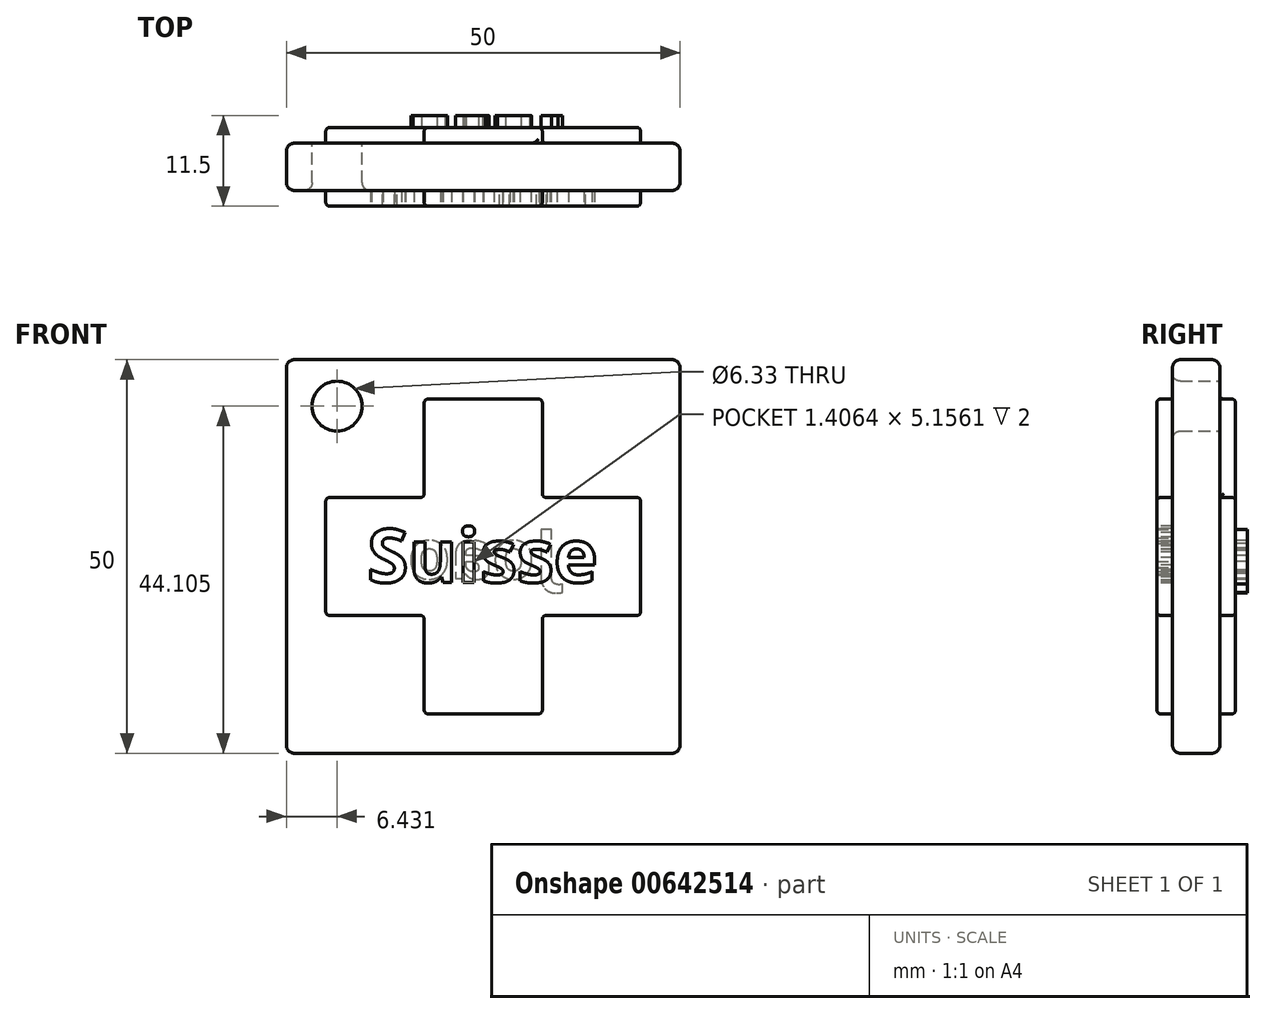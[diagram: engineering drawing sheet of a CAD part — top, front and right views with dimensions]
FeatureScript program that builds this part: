
annotation { "Feature Type Name" : "Feature", "Feature Type Description" : "" }
export const myFeature = defineFeature(function(context is Context, id is Id, definition is map)
    precondition{}
    {
        {
            var Q0;
            Q0=qCreatedBy(makeId("Front.planeOp"),FACE);
            var sketch = newSketch(context, id + "F0", { "sketchPlane" : qUnion([Q0])});
            skLineSegment(sketch, "E0.bottom", {"start": v(25, -25) * mm, "end": v(-25, -25) * mm});
            skLineSegment(sketch, "E0.top", {"start": v(25, 25) * mm, "end": v(-25, 25) * mm});
            skLineSegment(sketch, "E0.left", {"start": v(25, -25) * mm, "end": v(25, 25) * mm});
            skLineSegment(sketch, "E0.right", {"start": v(-25, -25) * mm, "end": v(-25, 25) * mm});
            skLineSegment(sketch, "E1.bottom", {"start": v(7.5, -20) * mm, "end": v(-7.5, -20) * mm});
            skLineSegment(sketch, "E1.top", {"start": v(7.5, 20) * mm, "end": v(-7.5, 20) * mm});
            skLineSegment(sketch, "E1.left", {"start": v(7.5, -20) * mm, "end": v(7.5, 20) * mm});
            skLineSegment(sketch, "E1.right", {"start": v(-7.5, -20) * mm, "end": v(-7.5, 20) * mm});
            skPoint(sketch, "E1.middle", {"position": v(0, 0) * mm});
            skLineSegment(sketch, "E2.bottom", {"start": v(-20, 7.5) * mm, "end": v(20, 7.5) * mm});
            skLineSegment(sketch, "E2.top", {"start": v(-20, -7.5) * mm, "end": v(20, -7.5) * mm});
            skLineSegment(sketch, "E2.left", {"start": v(-20, 7.5) * mm, "end": v(-20, -7.5) * mm});
            skLineSegment(sketch, "E2.right", {"start": v(20, 7.5) * mm, "end": v(20, -7.5) * mm});
            skSolve(sketch);
        }
        {
            var Q0;
            {var subQ0=sQuery(id+"F0.wireOp",EDGE,"E2.top");var subQ1=sQuery(id+"F0.wireOp",EDGE,"E1.left");var subQ2=makeQuery(id+"F0.imprint","INTERSECT",VERTEX,{"derivedFrom":[subQ1,subQ0]});Q0=makeQuery(id+"F0.imprint","IMPRINT",FACE,{"disambiguationData":[TD([[makeQuery(id+"F0.imprint","IMPRINT",EDGE,{"disambiguationData":[TD([[subQ2,-1.0]])],"derivedFrom":subQ1}),1.0]])]});}
            var Q1;
            {var subQ5=sQuery(id+"F0.wireOp",EDGE,"E2.left");Q1=makeQuery(id+"F0.imprint","IMPRINT",FACE,{"disambiguationData":[TD([[makeQuery(id+"F0.imprint","IMPRINT",EDGE,{"derivedFrom":subQ5}),1.0]])]});}
            var Q2;
            {var subQ5=sQuery(id+"F0.wireOp",EDGE,"E2.right");Q2=makeQuery(id+"F0.imprint","IMPRINT",FACE,{"disambiguationData":[TD([[makeQuery(id+"F0.imprint","IMPRINT",EDGE,{"derivedFrom":subQ5}),-1.0]])]});}
            var Q3;
            {var subQ0=sQuery(id+"F0.wireOp",EDGE,"E1.bottom");Q3=makeQuery(id+"F0.imprint","IMPRINT",FACE,{"disambiguationData":[TD([[makeQuery(id+"F0.imprint","IMPRINT",EDGE,{"derivedFrom":subQ0}),-1.0]])]});}
            var Q4;
            {var subQ0=sQuery(id+"F0.wireOp",EDGE,"E1.top");Q4=makeQuery(id+"F0.imprint","IMPRINT",FACE,{"disambiguationData":[TD([[makeQuery(id+"F0.imprint","IMPRINT",EDGE,{"derivedFrom":subQ0}),1.0]])]});}
            extrude(context, id + "F1", {"entities" : qUnion([Q0, Q1, Q2, Q3, Q4]), "endBound" : BoundingType.SYMMETRIC, "depth" : 10 * mm, "offsetDistance" : 25 * mm});
        }
        {
            var Q0;
            Q0=makeQuery(id+"F0.imprint","IMPRINT",FACE,{"disambiguationData":[TD([[makeQuery(id+"F0.imprint","IMPRINT",EDGE,{"derivedFrom":sQuery(id+"F0.wireOp",EDGE,"E0.bottom")}),-1.0]])]});
            extrude(context, id + "F2", {"entities" : qUnion([Q0]), "operationType" : NewBodyOperationType.ADD, "endBound" : BoundingType.SYMMETRIC, "depth" : 6 * mm, "offsetDistance" : 25 * mm});
        }
        {
            var Q0;
            Q0=makeQuery(id+"F1.opExtrude","CAP_FACE",FACE,{"disambiguationData":[OSD([sQuery(id+"F0.wireOp",EDGE,"E1.bottom"),sQuery(id+"F0.wireOp",EDGE,"E1.top"),sQuery(id+"F0.wireOp",EDGE,"E1.left"),sQuery(id+"F0.wireOp",EDGE,"E1.right"),sQuery(id+"F0.wireOp",EDGE,"E2.bottom"),sQuery(id+"F0.wireOp",EDGE,"E2.top"),sQuery(id+"F0.wireOp",EDGE,"E2.left"),sQuery(id+"F0.wireOp",EDGE,"E2.right")])],"isStart":true});
            var sketch = newSketch(context, id + "F3", { "sketchPlane" : qUnion([Q0])});
            skText(sketch, "E3", { "text": "Joao", "fontName": "OpenSans-Bold.ttf"});
            const initialGuessF3  = {"E3": [-0.00944, -0.00282, 1, 0, 0.0063]};
            skSetInitialGuess(sketch, initialGuessF3);
            skSolve(sketch);
        }
        {
            var Q0;
            Q0 = qSketchRegion(id + "F3", true);
            extrude(context, id + "F4", {"entities" : qUnion([Q0]), "operationType" : NewBodyOperationType.ADD, "endBound" : BoundingType.SYMMETRIC, "depth" : 3 * mm, "offsetDistance" : 25 * mm});
        }
        {
            var Q0;
            Q0=makeQuery(id+"F2.opExtrude","CAP_FACE",FACE,{"disambiguationData":[OSD([sQuery(id+"F0.wireOp",EDGE,"E0.bottom"),sQuery(id+"F0.wireOp",EDGE,"E0.top"),sQuery(id+"F0.wireOp",EDGE,"E0.left"),sQuery(id+"F0.wireOp",EDGE,"E0.right"),sQuery(id+"F0.wireOp",EDGE,"E1.bottom"),sQuery(id+"F0.wireOp",EDGE,"E1.top"),sQuery(id+"F0.wireOp",EDGE,"E1.left"),sQuery(id+"F0.wireOp",EDGE,"E1.right"),sQuery(id+"F0.wireOp",EDGE,"E2.bottom"),sQuery(id+"F0.wireOp",EDGE,"E2.top"),sQuery(id+"F0.wireOp",EDGE,"E2.left"),sQuery(id+"F0.wireOp",EDGE,"E2.right")])],"isStart":true});
            var sketch = newSketch(context, id + "F5", { "sketchPlane" : qUnion([Q0])});
            skCircle(sketch, "E4", {"center": v(18.57, 19.1) * mm, "radius": 3.17 * mm});
            skSolve(sketch);
        }
        {
            var Q0;
            Q0 = qSketchRegion(id + "F5", true);
            extrude(context, id + "F6", {"entities" : qUnion([Q0]), "operationType" : NewBodyOperationType.REMOVE, "oppositeDirection" : true, "depth" : 25 * mm, "offsetDistance" : 25 * mm});
        }
        {
            var Q0;
            Q0=makeQuery(id+"F2.opExtrude","CAP_EDGE",EDGE,{"disambiguationData":[OSD([sQuery(id+"F0.wireOp",EDGE,"E0.bottom")])],"isStart":false});
            var Q1;
            Q1=makeQuery(id+"F2.opExtrude","CAP_EDGE",EDGE,{"disambiguationData":[OSD([sQuery(id+"F0.wireOp",EDGE,"E0.left")])],"isStart":false});
            var Q2;
            Q2=makeQuery(id+"F2.opExtrude","CAP_EDGE",EDGE,{"disambiguationData":[OSD([sQuery(id+"F0.wireOp",EDGE,"E0.right")])],"isStart":false});
            var Q3;
            Q3=makeQuery(id+"F2.opExtrude","CAP_EDGE",EDGE,{"disambiguationData":[OSD([sQuery(id+"F0.wireOp",EDGE,"E0.top")])],"isStart":false});
            var Q4;
            Q4=makeQuery(id+"F2.opExtrude","SWEPT_EDGE",EDGE,{"disambiguationData":[OSD([sQuery(id+"F0.wireOp",EDGE,"E0.top"),sQuery(id+"F0.wireOp",EDGE,"E0.left")])]});
            var Q5;
            Q5=makeQuery(id+"F2.opExtrude","SWEPT_EDGE",EDGE,{"disambiguationData":[OSD([sQuery(id+"F0.wireOp",EDGE,"E0.bottom"),sQuery(id+"F0.wireOp",EDGE,"E0.left")])]});
            var Q6;
            Q6=makeQuery(id+"F2.opExtrude","SWEPT_EDGE",EDGE,{"disambiguationData":[OSD([sQuery(id+"F0.wireOp",EDGE,"E0.bottom"),sQuery(id+"F0.wireOp",EDGE,"E0.right")])]});
            var Q7;
            Q7=makeQuery(id+"F2.opExtrude","SWEPT_EDGE",EDGE,{"disambiguationData":[OSD([sQuery(id+"F0.wireOp",EDGE,"E0.top"),sQuery(id+"F0.wireOp",EDGE,"E0.right")])]});
            var Q8;
            Q8=makeQuery(id+"F2.opExtrude","CAP_EDGE",EDGE,{"disambiguationData":[OSD([sQuery(id+"F0.wireOp",EDGE,"E0.top")])],"isStart":true});
            var Q9;
            Q9=makeQuery(id+"F2.opExtrude","CAP_EDGE",EDGE,{"disambiguationData":[OSD([sQuery(id+"F0.wireOp",EDGE,"E0.right")])],"isStart":true});
            var Q10;
            Q10=makeQuery(id+"F2.opExtrude","CAP_EDGE",EDGE,{"disambiguationData":[OSD([sQuery(id+"F0.wireOp",EDGE,"E0.left")])],"isStart":true});
            var Q11;
            Q11=makeQuery(id+"F2.opExtrude","CAP_EDGE",EDGE,{"disambiguationData":[OSD([sQuery(id+"F0.wireOp",EDGE,"E0.bottom")])],"isStart":true});
            var Q12;
            Q12=makeQuery(id+"F6.boolean.opBoolean","COPY",EDGE,{"derivedFrom":makeQuery(id+"F6.opExtrude","CAP_EDGE",EDGE,{"disambiguationData":[OSD([sQuery(id+"F5.wireOp",EDGE,"E4")])],"isStart":true})});
            var Q13;
            Q13=makeQuery(id+"F6.boolean.opBoolean","INTERSECT",EDGE,{"derivedFrom":[makeQuery(id+"F2.opExtrude","CAP_FACE",FACE,{"disambiguationData":[OSD([sQuery(id+"F0.wireOp",EDGE,"E0.bottom"),sQuery(id+"F0.wireOp",EDGE,"E0.top"),sQuery(id+"F0.wireOp",EDGE,"E0.left"),sQuery(id+"F0.wireOp",EDGE,"E0.right"),sQuery(id+"F0.wireOp",EDGE,"E1.bottom"),sQuery(id+"F0.wireOp",EDGE,"E1.top"),sQuery(id+"F0.wireOp",EDGE,"E1.left"),sQuery(id+"F0.wireOp",EDGE,"E1.right"),sQuery(id+"F0.wireOp",EDGE,"E2.bottom"),sQuery(id+"F0.wireOp",EDGE,"E2.top"),sQuery(id+"F0.wireOp",EDGE,"E2.left"),sQuery(id+"F0.wireOp",EDGE,"E2.right")])],"isStart":false}),makeQuery(id+"F6.opExtrude","SWEPT_FACE",FACE,{"disambiguationData":[OSD([sQuery(id+"F5.wireOp",EDGE,"E4")])]})]});
            fillet(context, id + "F7", {"entities" : qUnion([Q0, Q1, Q2, Q3, Q4, Q5, Q6, Q7, Q8, Q9, Q10, Q11, Q12, Q13]), "radius" : 1 * mm, "tangentPropagation" : true, "allowEdgeOverflow" : false});
        }
        {
            var Q0;
            Q0=makeQuery(id+"F1.opExtrude","CAP_EDGE",EDGE,{"disambiguationData":[OSD([sQuery(id+"F0.wireOp",EDGE,"E2.left")])],"isStart":false});
            var Q1;
            {var subQ0=sQuery(id+"F0.wireOp",EDGE,"E2.right");var subQ1=sQuery(id+"F0.wireOp",EDGE,"E2.left");var subQ2=sQuery(id+"F0.wireOp",EDGE,"E2.top");var subQ3=sQuery(id+"F0.wireOp",EDGE,"E2.bottom");var subQ4=sQuery(id+"F0.wireOp",EDGE,"E1.right");var subQ5=sQuery(id+"F0.wireOp",EDGE,"E1.left");var subQ6=sQuery(id+"F0.wireOp",EDGE,"E1.top");var subQ7=sQuery(id+"F0.wireOp",EDGE,"E1.bottom");Q1=makeQuery(id+"F2.boolean.opBoolean","SPLIT",EDGE,{"disambiguationData":[TD([makeQuery(id+"F1.opExtrude","CAP_FACE",FACE,{"disambiguationData":[OSD([subQ7,subQ6,subQ5,subQ4,subQ3,subQ2,subQ1,subQ0])],"isStart":false})])],"derivedFrom":makeQuery(id+"F1.opExtrude","SWEPT_EDGE",EDGE,{"disambiguationData":[OSD([subQ3,subQ1])]})});}
            var Q2;
            {var subQ0=sQuery(id+"F0.wireOp",EDGE,"E2.bottom");Q2=makeQuery(id+"F1.opExtrude","CAP_EDGE",EDGE,{"disambiguationData":[OSD([subQ0]),TDD([makeQuery(id+"F0.imprint","IMPRINT",EDGE,{"disambiguationData":[TD([[makeQuery(id+"F0.imprint","INTERSECT",VERTEX,{"derivedFrom":[subQ0,sQuery(id+"F0.wireOp",EDGE,"E2.left")]}),-1.0]])],"derivedFrom":subQ0})])],"isStart":false});}
            var Q3;
            {var subQ0=sQuery(id+"F0.wireOp",EDGE,"E2.top");Q3=makeQuery(id+"F1.opExtrude","CAP_EDGE",EDGE,{"disambiguationData":[OSD([subQ0]),TDD([makeQuery(id+"F0.imprint","IMPRINT",EDGE,{"disambiguationData":[TD([[makeQuery(id+"F0.imprint","INTERSECT",VERTEX,{"derivedFrom":[subQ0,sQuery(id+"F0.wireOp",EDGE,"E2.left")]}),-1.0]])],"derivedFrom":subQ0})])],"isStart":false});}
            var Q4;
            {var subQ0=sQuery(id+"F0.wireOp",EDGE,"E1.right");Q4=makeQuery(id+"F1.opExtrude","CAP_EDGE",EDGE,{"disambiguationData":[OSD([subQ0]),TDD([makeQuery(id+"F0.imprint","IMPRINT",EDGE,{"disambiguationData":[TD([[makeQuery(id+"F0.imprint","INTERSECT",VERTEX,{"derivedFrom":[sQuery(id+"F0.wireOp",EDGE,"E1.bottom"),subQ0]}),-1.0]])],"derivedFrom":subQ0})])],"isStart":false});}
            var Q5;
            {var subQ0=sQuery(id+"F0.wireOp",EDGE,"E2.right");var subQ1=sQuery(id+"F0.wireOp",EDGE,"E2.left");var subQ2=sQuery(id+"F0.wireOp",EDGE,"E2.top");var subQ3=sQuery(id+"F0.wireOp",EDGE,"E2.bottom");var subQ4=sQuery(id+"F0.wireOp",EDGE,"E1.right");var subQ5=sQuery(id+"F0.wireOp",EDGE,"E1.left");var subQ6=sQuery(id+"F0.wireOp",EDGE,"E1.top");var subQ7=sQuery(id+"F0.wireOp",EDGE,"E1.bottom");Q5=makeQuery(id+"F2.boolean.opBoolean","SPLIT",EDGE,{"disambiguationData":[TD([makeQuery(id+"F1.opExtrude","CAP_FACE",FACE,{"disambiguationData":[OSD([subQ7,subQ6,subQ5,subQ4,subQ3,subQ2,subQ1,subQ0])],"isStart":false})])],"derivedFrom":makeQuery(id+"F1.opExtrude","SWEPT_EDGE",EDGE,{"disambiguationData":[OSD([subQ4,subQ2])]})});}
            var Q6;
            {var subQ0=sQuery(id+"F0.wireOp",EDGE,"E2.right");var subQ1=sQuery(id+"F0.wireOp",EDGE,"E2.left");var subQ2=sQuery(id+"F0.wireOp",EDGE,"E2.top");var subQ3=sQuery(id+"F0.wireOp",EDGE,"E2.bottom");var subQ4=sQuery(id+"F0.wireOp",EDGE,"E1.right");var subQ5=sQuery(id+"F0.wireOp",EDGE,"E1.left");var subQ6=sQuery(id+"F0.wireOp",EDGE,"E1.top");var subQ7=sQuery(id+"F0.wireOp",EDGE,"E1.bottom");Q6=makeQuery(id+"F2.boolean.opBoolean","SPLIT",EDGE,{"disambiguationData":[TD([makeQuery(id+"F1.opExtrude","CAP_FACE",FACE,{"disambiguationData":[OSD([subQ7,subQ6,subQ5,subQ4,subQ3,subQ2,subQ1,subQ0])],"isStart":false})])],"derivedFrom":makeQuery(id+"F1.opExtrude","SWEPT_EDGE",EDGE,{"disambiguationData":[OSD([subQ2,subQ1])]})});}
            var Q7;
            Q7=makeQuery(id+"F1.opExtrude","CAP_EDGE",EDGE,{"disambiguationData":[OSD([sQuery(id+"F0.wireOp",EDGE,"E1.bottom")])],"isStart":false});
            var Q8;
            {var subQ0=sQuery(id+"F0.wireOp",EDGE,"E1.bottom");var subQ1=sQuery(id+"F0.wireOp",EDGE,"E2.right");var subQ2=sQuery(id+"F0.wireOp",EDGE,"E2.left");var subQ3=sQuery(id+"F0.wireOp",EDGE,"E2.top");var subQ4=sQuery(id+"F0.wireOp",EDGE,"E2.bottom");var subQ5=sQuery(id+"F0.wireOp",EDGE,"E1.right");var subQ6=sQuery(id+"F0.wireOp",EDGE,"E1.left");var subQ7=sQuery(id+"F0.wireOp",EDGE,"E1.top");Q8=makeQuery(id+"F2.boolean.opBoolean","SPLIT",EDGE,{"disambiguationData":[TD([makeQuery(id+"F1.opExtrude","CAP_FACE",FACE,{"disambiguationData":[OSD([subQ0,subQ7,subQ6,subQ5,subQ4,subQ3,subQ2,subQ1])],"isStart":false})])],"derivedFrom":makeQuery(id+"F1.opExtrude","SWEPT_EDGE",EDGE,{"disambiguationData":[OSD([subQ0,subQ5])]})});}
            var Q9;
            {var subQ0=sQuery(id+"F0.wireOp",EDGE,"E1.left");Q9=makeQuery(id+"F1.opExtrude","CAP_EDGE",EDGE,{"disambiguationData":[OSD([subQ0]),TDD([makeQuery(id+"F0.imprint","IMPRINT",EDGE,{"disambiguationData":[TD([[makeQuery(id+"F0.imprint","INTERSECT",VERTEX,{"derivedFrom":[sQuery(id+"F0.wireOp",EDGE,"E1.bottom"),subQ0]}),-1.0]])],"derivedFrom":subQ0})])],"isStart":false});}
            var Q10;
            {var subQ0=sQuery(id+"F0.wireOp",EDGE,"E2.top");Q10=makeQuery(id+"F1.opExtrude","CAP_EDGE",EDGE,{"disambiguationData":[OSD([subQ0]),TDD([makeQuery(id+"F0.imprint","IMPRINT",EDGE,{"disambiguationData":[TD([[makeQuery(id+"F0.imprint","INTERSECT",VERTEX,{"derivedFrom":[subQ0,sQuery(id+"F0.wireOp",EDGE,"E2.right")]}),1.0]])],"derivedFrom":subQ0})])],"isStart":false});}
            var Q11;
            {var subQ0=sQuery(id+"F0.wireOp",EDGE,"E2.right");var subQ1=sQuery(id+"F0.wireOp",EDGE,"E2.left");var subQ2=sQuery(id+"F0.wireOp",EDGE,"E2.top");var subQ3=sQuery(id+"F0.wireOp",EDGE,"E2.bottom");var subQ4=sQuery(id+"F0.wireOp",EDGE,"E1.right");var subQ5=sQuery(id+"F0.wireOp",EDGE,"E1.left");var subQ6=sQuery(id+"F0.wireOp",EDGE,"E1.top");var subQ7=sQuery(id+"F0.wireOp",EDGE,"E1.bottom");Q11=makeQuery(id+"F2.boolean.opBoolean","SPLIT",EDGE,{"disambiguationData":[TD([makeQuery(id+"F1.opExtrude","CAP_FACE",FACE,{"disambiguationData":[OSD([subQ7,subQ6,subQ5,subQ4,subQ3,subQ2,subQ1,subQ0])],"isStart":false})])],"derivedFrom":makeQuery(id+"F1.opExtrude","SWEPT_EDGE",EDGE,{"disambiguationData":[OSD([subQ5,subQ2])]})});}
            var Q12;
            {var subQ0=sQuery(id+"F0.wireOp",EDGE,"E1.bottom");var subQ1=sQuery(id+"F0.wireOp",EDGE,"E2.right");var subQ2=sQuery(id+"F0.wireOp",EDGE,"E2.left");var subQ3=sQuery(id+"F0.wireOp",EDGE,"E2.top");var subQ4=sQuery(id+"F0.wireOp",EDGE,"E2.bottom");var subQ5=sQuery(id+"F0.wireOp",EDGE,"E1.right");var subQ6=sQuery(id+"F0.wireOp",EDGE,"E1.left");var subQ7=sQuery(id+"F0.wireOp",EDGE,"E1.top");Q12=makeQuery(id+"F2.boolean.opBoolean","SPLIT",EDGE,{"disambiguationData":[TD([makeQuery(id+"F1.opExtrude","CAP_FACE",FACE,{"disambiguationData":[OSD([subQ0,subQ7,subQ6,subQ5,subQ4,subQ3,subQ2,subQ1])],"isStart":false})])],"derivedFrom":makeQuery(id+"F1.opExtrude","SWEPT_EDGE",EDGE,{"disambiguationData":[OSD([subQ0,subQ6])]})});}
            var Q13;
            {var subQ0=sQuery(id+"F0.wireOp",EDGE,"E2.right");var subQ1=sQuery(id+"F0.wireOp",EDGE,"E2.left");var subQ2=sQuery(id+"F0.wireOp",EDGE,"E2.top");var subQ3=sQuery(id+"F0.wireOp",EDGE,"E2.bottom");var subQ4=sQuery(id+"F0.wireOp",EDGE,"E1.right");var subQ5=sQuery(id+"F0.wireOp",EDGE,"E1.left");var subQ6=sQuery(id+"F0.wireOp",EDGE,"E1.top");var subQ7=sQuery(id+"F0.wireOp",EDGE,"E1.bottom");Q13=makeQuery(id+"F2.boolean.opBoolean","SPLIT",EDGE,{"disambiguationData":[TD([makeQuery(id+"F1.opExtrude","CAP_FACE",FACE,{"disambiguationData":[OSD([subQ7,subQ6,subQ5,subQ4,subQ3,subQ2,subQ1,subQ0])],"isStart":false})])],"derivedFrom":makeQuery(id+"F1.opExtrude","SWEPT_EDGE",EDGE,{"disambiguationData":[OSD([subQ2,subQ0])]})});}
            var Q14;
            Q14=makeQuery(id+"F1.opExtrude","CAP_EDGE",EDGE,{"disambiguationData":[OSD([sQuery(id+"F0.wireOp",EDGE,"E2.right")])],"isStart":false});
            var Q15;
            {var subQ0=sQuery(id+"F0.wireOp",EDGE,"E2.right");var subQ1=sQuery(id+"F0.wireOp",EDGE,"E2.left");var subQ2=sQuery(id+"F0.wireOp",EDGE,"E2.top");var subQ3=sQuery(id+"F0.wireOp",EDGE,"E2.bottom");var subQ4=sQuery(id+"F0.wireOp",EDGE,"E1.right");var subQ5=sQuery(id+"F0.wireOp",EDGE,"E1.left");var subQ6=sQuery(id+"F0.wireOp",EDGE,"E1.top");var subQ7=sQuery(id+"F0.wireOp",EDGE,"E1.bottom");Q15=makeQuery(id+"F2.boolean.opBoolean","SPLIT",EDGE,{"disambiguationData":[TD([makeQuery(id+"F1.opExtrude","CAP_FACE",FACE,{"disambiguationData":[OSD([subQ7,subQ6,subQ5,subQ4,subQ3,subQ2,subQ1,subQ0])],"isStart":false})])],"derivedFrom":makeQuery(id+"F1.opExtrude","SWEPT_EDGE",EDGE,{"disambiguationData":[OSD([subQ3,subQ0])]})});}
            var Q16;
            {var subQ0=sQuery(id+"F0.wireOp",EDGE,"E2.bottom");Q16=makeQuery(id+"F1.opExtrude","CAP_EDGE",EDGE,{"disambiguationData":[OSD([subQ0]),TDD([makeQuery(id+"F0.imprint","IMPRINT",EDGE,{"disambiguationData":[TD([[makeQuery(id+"F0.imprint","INTERSECT",VERTEX,{"derivedFrom":[subQ0,sQuery(id+"F0.wireOp",EDGE,"E2.right")]}),1.0]])],"derivedFrom":subQ0})])],"isStart":false});}
            var Q17;
            {var subQ0=sQuery(id+"F0.wireOp",EDGE,"E2.right");var subQ1=sQuery(id+"F0.wireOp",EDGE,"E2.left");var subQ2=sQuery(id+"F0.wireOp",EDGE,"E2.top");var subQ3=sQuery(id+"F0.wireOp",EDGE,"E2.bottom");var subQ4=sQuery(id+"F0.wireOp",EDGE,"E1.right");var subQ5=sQuery(id+"F0.wireOp",EDGE,"E1.left");var subQ6=sQuery(id+"F0.wireOp",EDGE,"E1.top");var subQ7=sQuery(id+"F0.wireOp",EDGE,"E1.bottom");Q17=makeQuery(id+"F2.boolean.opBoolean","SPLIT",EDGE,{"disambiguationData":[TD([makeQuery(id+"F1.opExtrude","CAP_FACE",FACE,{"disambiguationData":[OSD([subQ7,subQ6,subQ5,subQ4,subQ3,subQ2,subQ1,subQ0])],"isStart":false})])],"derivedFrom":makeQuery(id+"F1.opExtrude","SWEPT_EDGE",EDGE,{"disambiguationData":[OSD([subQ5,subQ3])]})});}
            var Q18;
            {var subQ0=sQuery(id+"F0.wireOp",EDGE,"E1.left");Q18=makeQuery(id+"F1.opExtrude","CAP_EDGE",EDGE,{"disambiguationData":[OSD([subQ0]),TDD([makeQuery(id+"F0.imprint","IMPRINT",EDGE,{"disambiguationData":[TD([[makeQuery(id+"F0.imprint","INTERSECT",VERTEX,{"derivedFrom":[sQuery(id+"F0.wireOp",EDGE,"E1.top"),subQ0]}),1.0]])],"derivedFrom":subQ0})])],"isStart":false});}
            var Q19;
            {var subQ0=sQuery(id+"F0.wireOp",EDGE,"E2.right");var subQ1=sQuery(id+"F0.wireOp",EDGE,"E2.left");var subQ2=sQuery(id+"F0.wireOp",EDGE,"E2.top");var subQ3=sQuery(id+"F0.wireOp",EDGE,"E2.bottom");var subQ4=sQuery(id+"F0.wireOp",EDGE,"E1.right");var subQ5=sQuery(id+"F0.wireOp",EDGE,"E1.left");var subQ6=sQuery(id+"F0.wireOp",EDGE,"E1.top");var subQ7=sQuery(id+"F0.wireOp",EDGE,"E1.bottom");Q19=makeQuery(id+"F2.boolean.opBoolean","SPLIT",EDGE,{"disambiguationData":[TD([makeQuery(id+"F1.opExtrude","CAP_FACE",FACE,{"disambiguationData":[OSD([subQ7,subQ6,subQ5,subQ4,subQ3,subQ2,subQ1,subQ0])],"isStart":false})])],"derivedFrom":makeQuery(id+"F1.opExtrude","SWEPT_EDGE",EDGE,{"disambiguationData":[OSD([subQ6,subQ5])]})});}
            var Q20;
            Q20=makeQuery(id+"F1.opExtrude","CAP_EDGE",EDGE,{"disambiguationData":[OSD([sQuery(id+"F0.wireOp",EDGE,"E1.top")])],"isStart":false});
            var Q21;
            {var subQ0=sQuery(id+"F0.wireOp",EDGE,"E1.right");Q21=makeQuery(id+"F1.opExtrude","CAP_EDGE",EDGE,{"disambiguationData":[OSD([subQ0]),TDD([makeQuery(id+"F0.imprint","IMPRINT",EDGE,{"disambiguationData":[TD([[makeQuery(id+"F0.imprint","INTERSECT",VERTEX,{"derivedFrom":[sQuery(id+"F0.wireOp",EDGE,"E1.top"),subQ0]}),1.0]])],"derivedFrom":subQ0})])],"isStart":false});}
            var Q22;
            {var subQ0=sQuery(id+"F0.wireOp",EDGE,"E2.right");var subQ1=sQuery(id+"F0.wireOp",EDGE,"E2.left");var subQ2=sQuery(id+"F0.wireOp",EDGE,"E2.top");var subQ3=sQuery(id+"F0.wireOp",EDGE,"E2.bottom");var subQ4=sQuery(id+"F0.wireOp",EDGE,"E1.right");var subQ5=sQuery(id+"F0.wireOp",EDGE,"E1.left");var subQ6=sQuery(id+"F0.wireOp",EDGE,"E1.top");var subQ7=sQuery(id+"F0.wireOp",EDGE,"E1.bottom");Q22=makeQuery(id+"F2.boolean.opBoolean","SPLIT",EDGE,{"disambiguationData":[TD([makeQuery(id+"F1.opExtrude","CAP_FACE",FACE,{"disambiguationData":[OSD([subQ7,subQ6,subQ5,subQ4,subQ3,subQ2,subQ1,subQ0])],"isStart":false})])],"derivedFrom":makeQuery(id+"F1.opExtrude","SWEPT_EDGE",EDGE,{"disambiguationData":[OSD([subQ6,subQ4])]})});}
            var Q23;
            {var subQ0=sQuery(id+"F0.wireOp",EDGE,"E2.right");var subQ1=sQuery(id+"F0.wireOp",EDGE,"E2.left");var subQ2=sQuery(id+"F0.wireOp",EDGE,"E2.top");var subQ3=sQuery(id+"F0.wireOp",EDGE,"E2.bottom");var subQ4=sQuery(id+"F0.wireOp",EDGE,"E1.right");var subQ5=sQuery(id+"F0.wireOp",EDGE,"E1.left");var subQ6=sQuery(id+"F0.wireOp",EDGE,"E1.top");var subQ7=sQuery(id+"F0.wireOp",EDGE,"E1.bottom");Q23=makeQuery(id+"F2.boolean.opBoolean","SPLIT",EDGE,{"disambiguationData":[TD([makeQuery(id+"F1.opExtrude","CAP_FACE",FACE,{"disambiguationData":[OSD([subQ7,subQ6,subQ5,subQ4,subQ3,subQ2,subQ1,subQ0])],"isStart":false})])],"derivedFrom":makeQuery(id+"F1.opExtrude","SWEPT_EDGE",EDGE,{"disambiguationData":[OSD([subQ4,subQ3])]})});}
            var Q24;
            {var subQ0=sQuery(id+"F0.wireOp",EDGE,"E1.left");Q24=makeQuery(id+"F1.opExtrude","CAP_EDGE",EDGE,{"disambiguationData":[OSD([subQ0]),TDD([makeQuery(id+"F0.imprint","IMPRINT",EDGE,{"disambiguationData":[TD([[makeQuery(id+"F0.imprint","INTERSECT",VERTEX,{"derivedFrom":[sQuery(id+"F0.wireOp",EDGE,"E1.top"),subQ0]}),1.0]])],"derivedFrom":subQ0})])],"isStart":true});}
            var Q25;
            {var subQ0=sQuery(id+"F0.wireOp",EDGE,"E1.right");Q25=makeQuery(id+"F1.opExtrude","CAP_EDGE",EDGE,{"disambiguationData":[OSD([subQ0]),TDD([makeQuery(id+"F0.imprint","IMPRINT",EDGE,{"disambiguationData":[TD([[makeQuery(id+"F0.imprint","INTERSECT",VERTEX,{"derivedFrom":[sQuery(id+"F0.wireOp",EDGE,"E1.top"),subQ0]}),1.0]])],"derivedFrom":subQ0})])],"isStart":true});}
            var Q26;
            Q26=makeQuery(id+"F1.opExtrude","CAP_EDGE",EDGE,{"disambiguationData":[OSD([sQuery(id+"F0.wireOp",EDGE,"E1.top")])],"isStart":true});
            var Q27;
            {var subQ0=sQuery(id+"F0.wireOp",EDGE,"E2.bottom");Q27=makeQuery(id+"F1.opExtrude","CAP_EDGE",EDGE,{"disambiguationData":[OSD([subQ0]),TDD([makeQuery(id+"F0.imprint","IMPRINT",EDGE,{"disambiguationData":[TD([[makeQuery(id+"F0.imprint","INTERSECT",VERTEX,{"derivedFrom":[subQ0,sQuery(id+"F0.wireOp",EDGE,"E2.right")]}),1.0]])],"derivedFrom":subQ0})])],"isStart":true});}
            var Q28;
            Q28=makeQuery(id+"F1.opExtrude","CAP_EDGE",EDGE,{"disambiguationData":[OSD([sQuery(id+"F0.wireOp",EDGE,"E2.right")])],"isStart":true});
            var Q29;
            {var subQ0=sQuery(id+"F0.wireOp",EDGE,"E2.top");Q29=makeQuery(id+"F1.opExtrude","CAP_EDGE",EDGE,{"disambiguationData":[OSD([subQ0]),TDD([makeQuery(id+"F0.imprint","IMPRINT",EDGE,{"disambiguationData":[TD([[makeQuery(id+"F0.imprint","INTERSECT",VERTEX,{"derivedFrom":[subQ0,sQuery(id+"F0.wireOp",EDGE,"E2.right")]}),1.0]])],"derivedFrom":subQ0})])],"isStart":true});}
            var Q30;
            {var subQ0=sQuery(id+"F0.wireOp",EDGE,"E1.left");Q30=makeQuery(id+"F1.opExtrude","CAP_EDGE",EDGE,{"disambiguationData":[OSD([subQ0]),TDD([makeQuery(id+"F0.imprint","IMPRINT",EDGE,{"disambiguationData":[TD([[makeQuery(id+"F0.imprint","INTERSECT",VERTEX,{"derivedFrom":[sQuery(id+"F0.wireOp",EDGE,"E1.bottom"),subQ0]}),-1.0]])],"derivedFrom":subQ0})])],"isStart":true});}
            var Q31;
            Q31=makeQuery(id+"F1.opExtrude","CAP_EDGE",EDGE,{"disambiguationData":[OSD([sQuery(id+"F0.wireOp",EDGE,"E1.bottom")])],"isStart":true});
            var Q32;
            {var subQ0=sQuery(id+"F0.wireOp",EDGE,"E2.right");var subQ1=sQuery(id+"F0.wireOp",EDGE,"E2.left");var subQ2=sQuery(id+"F0.wireOp",EDGE,"E2.top");var subQ3=sQuery(id+"F0.wireOp",EDGE,"E2.bottom");var subQ4=sQuery(id+"F0.wireOp",EDGE,"E1.right");var subQ5=sQuery(id+"F0.wireOp",EDGE,"E1.left");var subQ6=sQuery(id+"F0.wireOp",EDGE,"E1.top");var subQ7=sQuery(id+"F0.wireOp",EDGE,"E1.bottom");Q32=makeQuery(id+"F2.boolean.opBoolean","SPLIT",EDGE,{"disambiguationData":[TD([makeQuery(id+"F1.opExtrude","CAP_FACE",FACE,{"disambiguationData":[OSD([subQ7,subQ6,subQ5,subQ4,subQ3,subQ2,subQ1,subQ0])],"isStart":true})])],"derivedFrom":makeQuery(id+"F1.opExtrude","SWEPT_EDGE",EDGE,{"disambiguationData":[OSD([subQ4,subQ2])]})});}
            var Q33;
            {var subQ0=sQuery(id+"F0.wireOp",EDGE,"E2.top");Q33=makeQuery(id+"F1.opExtrude","CAP_EDGE",EDGE,{"disambiguationData":[OSD([subQ0]),TDD([makeQuery(id+"F0.imprint","IMPRINT",EDGE,{"disambiguationData":[TD([[makeQuery(id+"F0.imprint","INTERSECT",VERTEX,{"derivedFrom":[subQ0,sQuery(id+"F0.wireOp",EDGE,"E2.left")]}),-1.0]])],"derivedFrom":subQ0})])],"isStart":true});}
            var Q34;
            {var subQ0=sQuery(id+"F0.wireOp",EDGE,"E1.right");Q34=makeQuery(id+"F1.opExtrude","CAP_EDGE",EDGE,{"disambiguationData":[OSD([subQ0]),TDD([makeQuery(id+"F0.imprint","IMPRINT",EDGE,{"disambiguationData":[TD([[makeQuery(id+"F0.imprint","INTERSECT",VERTEX,{"derivedFrom":[sQuery(id+"F0.wireOp",EDGE,"E1.bottom"),subQ0]}),-1.0]])],"derivedFrom":subQ0})])],"isStart":true});}
            var Q35;
            Q35=makeQuery(id+"F1.opExtrude","CAP_EDGE",EDGE,{"disambiguationData":[OSD([sQuery(id+"F0.wireOp",EDGE,"E2.left")])],"isStart":true});
            var Q36;
            {var subQ0=sQuery(id+"F0.wireOp",EDGE,"E2.bottom");Q36=makeQuery(id+"F1.opExtrude","CAP_EDGE",EDGE,{"disambiguationData":[OSD([subQ0]),TDD([makeQuery(id+"F0.imprint","IMPRINT",EDGE,{"disambiguationData":[TD([[makeQuery(id+"F0.imprint","INTERSECT",VERTEX,{"derivedFrom":[subQ0,sQuery(id+"F0.wireOp",EDGE,"E2.left")]}),-1.0]])],"derivedFrom":subQ0})])],"isStart":true});}
            var Q37;
            {var subQ0=sQuery(id+"F0.wireOp",EDGE,"E2.right");var subQ1=sQuery(id+"F0.wireOp",EDGE,"E2.left");var subQ2=sQuery(id+"F0.wireOp",EDGE,"E2.top");var subQ3=sQuery(id+"F0.wireOp",EDGE,"E2.bottom");var subQ4=sQuery(id+"F0.wireOp",EDGE,"E1.right");var subQ5=sQuery(id+"F0.wireOp",EDGE,"E1.left");var subQ6=sQuery(id+"F0.wireOp",EDGE,"E1.top");var subQ7=sQuery(id+"F0.wireOp",EDGE,"E1.bottom");Q37=makeQuery(id+"F2.boolean.opBoolean","SPLIT",EDGE,{"disambiguationData":[TD([makeQuery(id+"F1.opExtrude","CAP_FACE",FACE,{"disambiguationData":[OSD([subQ7,subQ6,subQ5,subQ4,subQ3,subQ2,subQ1,subQ0])],"isStart":true})])],"derivedFrom":makeQuery(id+"F1.opExtrude","SWEPT_EDGE",EDGE,{"disambiguationData":[OSD([subQ4,subQ3])]})});}
            var Q38;
            {var subQ0=sQuery(id+"F0.wireOp",EDGE,"E2.right");var subQ1=sQuery(id+"F0.wireOp",EDGE,"E2.left");var subQ2=sQuery(id+"F0.wireOp",EDGE,"E2.top");var subQ3=sQuery(id+"F0.wireOp",EDGE,"E2.bottom");var subQ4=sQuery(id+"F0.wireOp",EDGE,"E1.right");var subQ5=sQuery(id+"F0.wireOp",EDGE,"E1.left");var subQ6=sQuery(id+"F0.wireOp",EDGE,"E1.top");var subQ7=sQuery(id+"F0.wireOp",EDGE,"E1.bottom");Q38=makeQuery(id+"F2.boolean.opBoolean","SPLIT",EDGE,{"disambiguationData":[TD([makeQuery(id+"F1.opExtrude","CAP_FACE",FACE,{"disambiguationData":[OSD([subQ7,subQ6,subQ5,subQ4,subQ3,subQ2,subQ1,subQ0])],"isStart":true})])],"derivedFrom":makeQuery(id+"F1.opExtrude","SWEPT_EDGE",EDGE,{"disambiguationData":[OSD([subQ3,subQ1])]})});}
            var Q39;
            {var subQ0=sQuery(id+"F0.wireOp",EDGE,"E2.right");var subQ1=sQuery(id+"F0.wireOp",EDGE,"E2.left");var subQ2=sQuery(id+"F0.wireOp",EDGE,"E2.top");var subQ3=sQuery(id+"F0.wireOp",EDGE,"E2.bottom");var subQ4=sQuery(id+"F0.wireOp",EDGE,"E1.right");var subQ5=sQuery(id+"F0.wireOp",EDGE,"E1.left");var subQ6=sQuery(id+"F0.wireOp",EDGE,"E1.top");var subQ7=sQuery(id+"F0.wireOp",EDGE,"E1.bottom");Q39=makeQuery(id+"F2.boolean.opBoolean","SPLIT",EDGE,{"disambiguationData":[TD([makeQuery(id+"F1.opExtrude","CAP_FACE",FACE,{"disambiguationData":[OSD([subQ7,subQ6,subQ5,subQ4,subQ3,subQ2,subQ1,subQ0])],"isStart":true})])],"derivedFrom":makeQuery(id+"F1.opExtrude","SWEPT_EDGE",EDGE,{"disambiguationData":[OSD([subQ2,subQ1])]})});}
            var Q40;
            {var subQ0=sQuery(id+"F0.wireOp",EDGE,"E1.bottom");var subQ1=sQuery(id+"F0.wireOp",EDGE,"E2.right");var subQ2=sQuery(id+"F0.wireOp",EDGE,"E2.left");var subQ3=sQuery(id+"F0.wireOp",EDGE,"E2.top");var subQ4=sQuery(id+"F0.wireOp",EDGE,"E2.bottom");var subQ5=sQuery(id+"F0.wireOp",EDGE,"E1.right");var subQ6=sQuery(id+"F0.wireOp",EDGE,"E1.left");var subQ7=sQuery(id+"F0.wireOp",EDGE,"E1.top");Q40=makeQuery(id+"F2.boolean.opBoolean","SPLIT",EDGE,{"disambiguationData":[TD([makeQuery(id+"F1.opExtrude","CAP_FACE",FACE,{"disambiguationData":[OSD([subQ0,subQ7,subQ6,subQ5,subQ4,subQ3,subQ2,subQ1])],"isStart":true})])],"derivedFrom":makeQuery(id+"F1.opExtrude","SWEPT_EDGE",EDGE,{"disambiguationData":[OSD([subQ0,subQ5])]})});}
            var Q41;
            {var subQ0=sQuery(id+"F0.wireOp",EDGE,"E1.bottom");var subQ1=sQuery(id+"F0.wireOp",EDGE,"E2.right");var subQ2=sQuery(id+"F0.wireOp",EDGE,"E2.left");var subQ3=sQuery(id+"F0.wireOp",EDGE,"E2.top");var subQ4=sQuery(id+"F0.wireOp",EDGE,"E2.bottom");var subQ5=sQuery(id+"F0.wireOp",EDGE,"E1.right");var subQ6=sQuery(id+"F0.wireOp",EDGE,"E1.left");var subQ7=sQuery(id+"F0.wireOp",EDGE,"E1.top");Q41=makeQuery(id+"F2.boolean.opBoolean","SPLIT",EDGE,{"disambiguationData":[TD([makeQuery(id+"F1.opExtrude","CAP_FACE",FACE,{"disambiguationData":[OSD([subQ0,subQ7,subQ6,subQ5,subQ4,subQ3,subQ2,subQ1])],"isStart":true})])],"derivedFrom":makeQuery(id+"F1.opExtrude","SWEPT_EDGE",EDGE,{"disambiguationData":[OSD([subQ0,subQ6])]})});}
            var Q42;
            {var subQ0=sQuery(id+"F0.wireOp",EDGE,"E2.right");var subQ1=sQuery(id+"F0.wireOp",EDGE,"E2.left");var subQ2=sQuery(id+"F0.wireOp",EDGE,"E2.top");var subQ3=sQuery(id+"F0.wireOp",EDGE,"E2.bottom");var subQ4=sQuery(id+"F0.wireOp",EDGE,"E1.right");var subQ5=sQuery(id+"F0.wireOp",EDGE,"E1.left");var subQ6=sQuery(id+"F0.wireOp",EDGE,"E1.top");var subQ7=sQuery(id+"F0.wireOp",EDGE,"E1.bottom");Q42=makeQuery(id+"F2.boolean.opBoolean","SPLIT",EDGE,{"disambiguationData":[TD([makeQuery(id+"F1.opExtrude","CAP_FACE",FACE,{"disambiguationData":[OSD([subQ7,subQ6,subQ5,subQ4,subQ3,subQ2,subQ1,subQ0])],"isStart":true})])],"derivedFrom":makeQuery(id+"F1.opExtrude","SWEPT_EDGE",EDGE,{"disambiguationData":[OSD([subQ5,subQ2])]})});}
            var Q43;
            {var subQ0=sQuery(id+"F0.wireOp",EDGE,"E2.right");var subQ1=sQuery(id+"F0.wireOp",EDGE,"E2.left");var subQ2=sQuery(id+"F0.wireOp",EDGE,"E2.top");var subQ3=sQuery(id+"F0.wireOp",EDGE,"E2.bottom");var subQ4=sQuery(id+"F0.wireOp",EDGE,"E1.right");var subQ5=sQuery(id+"F0.wireOp",EDGE,"E1.left");var subQ6=sQuery(id+"F0.wireOp",EDGE,"E1.top");var subQ7=sQuery(id+"F0.wireOp",EDGE,"E1.bottom");Q43=makeQuery(id+"F2.boolean.opBoolean","SPLIT",EDGE,{"disambiguationData":[TD([makeQuery(id+"F1.opExtrude","CAP_FACE",FACE,{"disambiguationData":[OSD([subQ7,subQ6,subQ5,subQ4,subQ3,subQ2,subQ1,subQ0])],"isStart":true})])],"derivedFrom":makeQuery(id+"F1.opExtrude","SWEPT_EDGE",EDGE,{"disambiguationData":[OSD([subQ2,subQ0])]})});}
            var Q44;
            {var subQ0=sQuery(id+"F0.wireOp",EDGE,"E2.right");var subQ1=sQuery(id+"F0.wireOp",EDGE,"E2.left");var subQ2=sQuery(id+"F0.wireOp",EDGE,"E2.top");var subQ3=sQuery(id+"F0.wireOp",EDGE,"E2.bottom");var subQ4=sQuery(id+"F0.wireOp",EDGE,"E1.right");var subQ5=sQuery(id+"F0.wireOp",EDGE,"E1.left");var subQ6=sQuery(id+"F0.wireOp",EDGE,"E1.top");var subQ7=sQuery(id+"F0.wireOp",EDGE,"E1.bottom");Q44=makeQuery(id+"F2.boolean.opBoolean","SPLIT",EDGE,{"disambiguationData":[TD([makeQuery(id+"F1.opExtrude","CAP_FACE",FACE,{"disambiguationData":[OSD([subQ7,subQ6,subQ5,subQ4,subQ3,subQ2,subQ1,subQ0])],"isStart":true})])],"derivedFrom":makeQuery(id+"F1.opExtrude","SWEPT_EDGE",EDGE,{"disambiguationData":[OSD([subQ3,subQ0])]})});}
            var Q45;
            {var subQ0=sQuery(id+"F0.wireOp",EDGE,"E2.right");var subQ1=sQuery(id+"F0.wireOp",EDGE,"E2.left");var subQ2=sQuery(id+"F0.wireOp",EDGE,"E2.top");var subQ3=sQuery(id+"F0.wireOp",EDGE,"E2.bottom");var subQ4=sQuery(id+"F0.wireOp",EDGE,"E1.right");var subQ5=sQuery(id+"F0.wireOp",EDGE,"E1.left");var subQ6=sQuery(id+"F0.wireOp",EDGE,"E1.top");var subQ7=sQuery(id+"F0.wireOp",EDGE,"E1.bottom");Q45=makeQuery(id+"F2.boolean.opBoolean","SPLIT",EDGE,{"disambiguationData":[TD([makeQuery(id+"F1.opExtrude","CAP_FACE",FACE,{"disambiguationData":[OSD([subQ7,subQ6,subQ5,subQ4,subQ3,subQ2,subQ1,subQ0])],"isStart":true})])],"derivedFrom":makeQuery(id+"F1.opExtrude","SWEPT_EDGE",EDGE,{"disambiguationData":[OSD([subQ5,subQ3])]})});}
            var Q46;
            {var subQ0=sQuery(id+"F0.wireOp",EDGE,"E2.right");var subQ1=sQuery(id+"F0.wireOp",EDGE,"E2.left");var subQ2=sQuery(id+"F0.wireOp",EDGE,"E2.top");var subQ3=sQuery(id+"F0.wireOp",EDGE,"E2.bottom");var subQ4=sQuery(id+"F0.wireOp",EDGE,"E1.right");var subQ5=sQuery(id+"F0.wireOp",EDGE,"E1.left");var subQ6=sQuery(id+"F0.wireOp",EDGE,"E1.top");var subQ7=sQuery(id+"F0.wireOp",EDGE,"E1.bottom");Q46=makeQuery(id+"F2.boolean.opBoolean","SPLIT",FACE,{"disambiguationData":[TD([makeQuery(id+"F1.opExtrude","CAP_FACE",FACE,{"disambiguationData":[OSD([subQ7,subQ6,subQ5,subQ4,subQ3,subQ2,subQ1,subQ0])],"isStart":true})])],"derivedFrom":makeQuery(id+"F1.opExtrude","SWEPT_FACE",FACE,{"disambiguationData":[OSD([subQ5]),TDD([makeQuery(id+"F0.imprint","IMPRINT",EDGE,{"disambiguationData":[TD([[makeQuery(id+"F0.imprint","INTERSECT",VERTEX,{"derivedFrom":[subQ6,subQ5]}),1.0]])],"derivedFrom":subQ5})])]})});}
            var Q47;
            {var subQ0=sQuery(id+"F0.wireOp",EDGE,"E2.right");var subQ1=sQuery(id+"F0.wireOp",EDGE,"E2.left");var subQ2=sQuery(id+"F0.wireOp",EDGE,"E2.top");var subQ3=sQuery(id+"F0.wireOp",EDGE,"E2.bottom");var subQ4=sQuery(id+"F0.wireOp",EDGE,"E1.right");var subQ5=sQuery(id+"F0.wireOp",EDGE,"E1.left");var subQ6=sQuery(id+"F0.wireOp",EDGE,"E1.top");var subQ7=sQuery(id+"F0.wireOp",EDGE,"E1.bottom");Q47=makeQuery(id+"F2.boolean.opBoolean","SPLIT",EDGE,{"disambiguationData":[TD([makeQuery(id+"F1.opExtrude","CAP_FACE",FACE,{"disambiguationData":[OSD([subQ7,subQ6,subQ5,subQ4,subQ3,subQ2,subQ1,subQ0])],"isStart":true})])],"derivedFrom":makeQuery(id+"F1.opExtrude","SWEPT_EDGE",EDGE,{"disambiguationData":[OSD([subQ6,subQ4])]})});}
            fillet(context, id + "F8", {"entities" : qUnion([Q0, Q1, Q2, Q3, Q4, Q5, Q6, Q7, Q8, Q9, Q10, Q11, Q12, Q13, Q14, Q15, Q16, Q17, Q18, Q19, Q20, Q21, Q22, Q23, Q24, Q25, Q26, Q27, Q28, Q29, Q30, Q31, Q32, Q33, Q34, Q35, Q36, Q37, Q38, Q39, Q40, Q41, Q42, Q43, Q44, Q45, Q46, Q47]), "radius" : 0.5 * mm, "tangentPropagation" : true, "allowEdgeOverflow" : false});
        }
        {
            var Q0;
            Q0=makeQuery(id+"F1.opExtrude","CAP_FACE",FACE,{"disambiguationData":[OSD([sQuery(id+"F0.wireOp",EDGE,"E1.bottom"),sQuery(id+"F0.wireOp",EDGE,"E1.top"),sQuery(id+"F0.wireOp",EDGE,"E1.left"),sQuery(id+"F0.wireOp",EDGE,"E1.right"),sQuery(id+"F0.wireOp",EDGE,"E2.bottom"),sQuery(id+"F0.wireOp",EDGE,"E2.top"),sQuery(id+"F0.wireOp",EDGE,"E2.left"),sQuery(id+"F0.wireOp",EDGE,"E2.right")])],"isStart":false});
            var sketch = newSketch(context, id + "F9", { "sketchPlane" : qUnion([Q0])});
            skText(sketch, "E5", { "text": "Suisse", "fontName": "OpenSans-Bold.ttf"});
            const initialGuessF9  = {"E5": [-0.01472, -0.00329, 1, 0, 0.0068]};
            skSetInitialGuess(sketch, initialGuessF9);
            skSolve(sketch);
        }
        {
            var Q0;
            Q0 = qSketchRegion(id + "F9", true);
            extrude(context, id + "F10", {"entities" : qUnion([Q0]), "operationType" : NewBodyOperationType.REMOVE, "oppositeDirection" : true, "depth" : 2 * mm, "offsetDistance" : 25 * mm});
        }
    });
